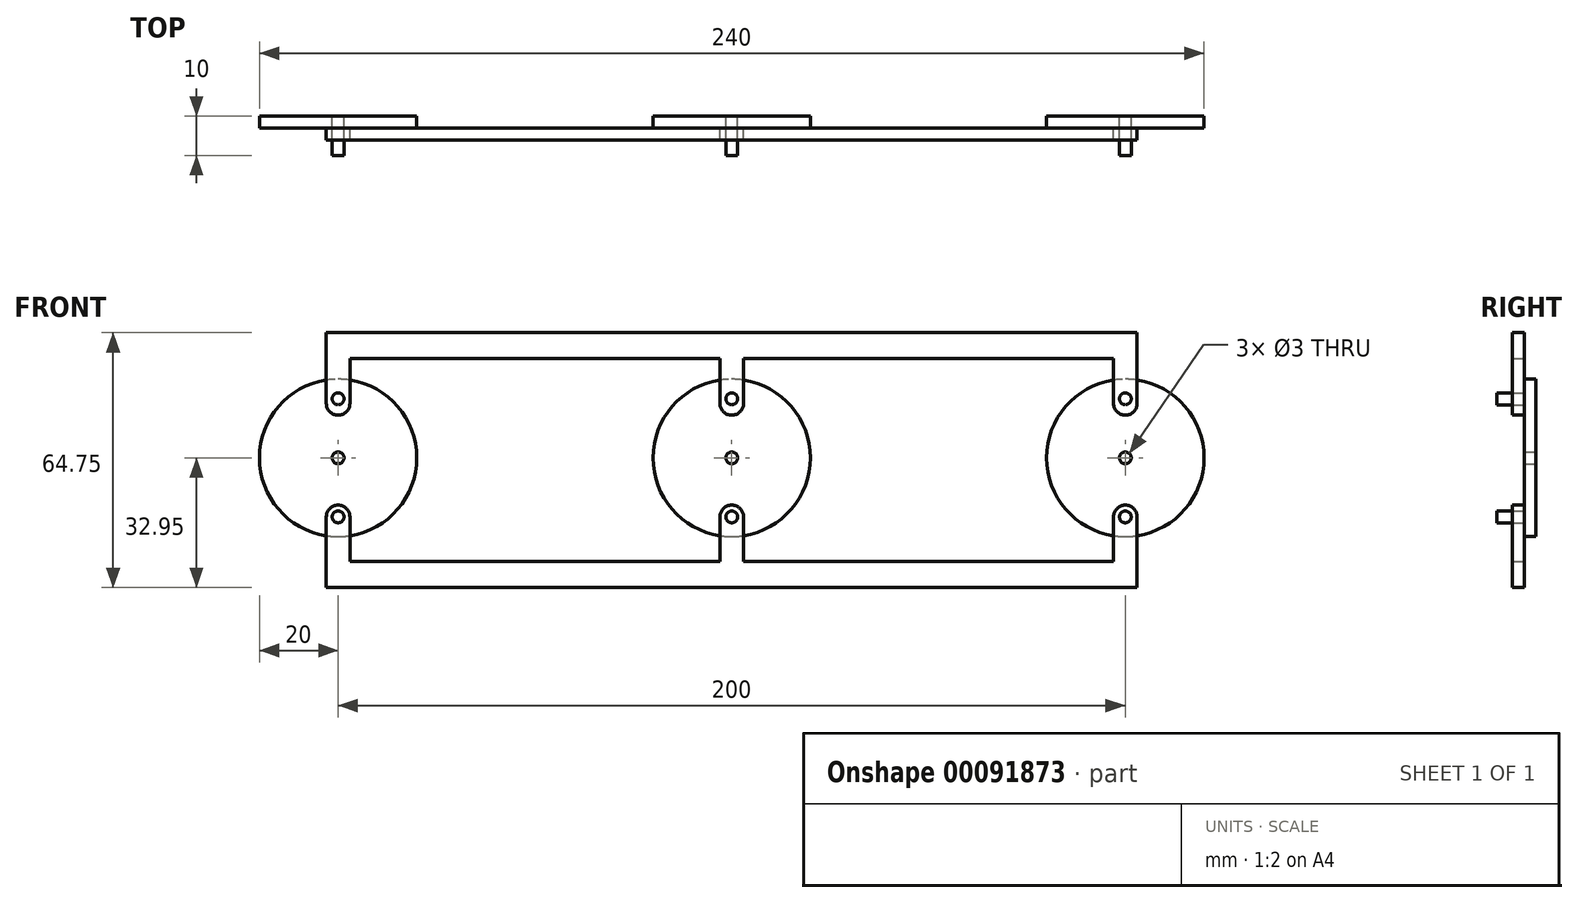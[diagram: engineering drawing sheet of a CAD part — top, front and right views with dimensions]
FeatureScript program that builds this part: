
annotation { "Feature Type Name" : "Feature", "Feature Type Description" : "" }
export const myFeature = defineFeature(function(context is Context, id is Id, definition is map)
    precondition{}
    {
        {
            var Q0;
            Q0=qCreatedBy(makeId("Front.planeOp"),FACE);
            var sketch = newSketch(context, id + "F0", { "sketchPlane" : qUnion([Q0])});
            skLineSegment(sketch, "E0", {"start": v(0, 45.39) * mm, "end": v(-100, 45.39) * mm});
            skCircle(sketch, "E1", {"center": v(-100, 0) * mm, "radius": 20 * mm});
            skCircle(sketch, "E2.1.0.0", {"center": v(0, 0) * mm, "radius": 20 * mm});
            skCircle(sketch, "E2.2.0.0", {"center": v(100, 0) * mm, "radius": 20 * mm});
            skLineSegment(sketch, "E2.direction1", {"start": v(-100, 0) * mm, "end": v(0, 0) * mm, "construction": true});
            skCircle(sketch, "E3", {"center": v(-100, 15) * mm, "radius": 1.5 * mm});
            skCircle(sketch, "E4", {"center": v(-100, -15) * mm, "radius": 1.5 * mm});
            skCircle(sketch, "E5.1.0.0", {"center": v(0, 15) * mm, "radius": 1.5 * mm});
            skCircle(sketch, "E5.1.0.1", {"center": v(0, -15) * mm, "radius": 1.5 * mm});
            skCircle(sketch, "E5.2.0.0", {"center": v(100, 15) * mm, "radius": 1.5 * mm});
            skCircle(sketch, "E5.2.0.1", {"center": v(100, -15) * mm, "radius": 1.5 * mm});
            skLineSegment(sketch, "E5.direction1", {"start": v(-100, 15) * mm, "end": v(0, 15) * mm, "construction": true});
            skCircle(sketch, "E6", {"center": v(-100, 0) * mm, "radius": 1.5 * mm});
            skCircle(sketch, "E7.1.0.0", {"center": v(0, 0) * mm, "radius": 1.5 * mm});
            skCircle(sketch, "E7.2.0.0", {"center": v(100, 0) * mm, "radius": 1.5 * mm});
            skSolve(sketch);
        }
        {
            var Q0;
            Q0 = qSketchRegion(id + "F0", true);
            extrude(context, id + "F1", {"entities" : qUnion([Q0]), "depth" : 3 * mm});
        }
        {
            var Q0;
            Q0=makeQuery(id+"F0.imprint","IMPRINT",FACE,{"disambiguationData":[TD([[makeQuery(id+"F0.imprint","IMPRINT",EDGE,{"derivedFrom":sQuery(id+"F0.wireOp",EDGE,"E3")}),1.0]])]});
            var Q1;
            Q1=makeQuery(id+"F0.imprint","IMPRINT",FACE,{"disambiguationData":[TD([[makeQuery(id+"F0.imprint","IMPRINT",EDGE,{"derivedFrom":sQuery(id+"F0.wireOp",EDGE,"E4")}),1.0]])]});
            var Q2;
            Q2=makeQuery(id+"F0.imprint","IMPRINT",FACE,{"disambiguationData":[TD([[makeQuery(id+"F0.imprint","IMPRINT",EDGE,{"derivedFrom":sQuery(id+"F0.wireOp",EDGE,"E5.2.0.0")}),1.0]])]});
            var Q3;
            Q3=makeQuery(id+"F0.imprint","IMPRINT",FACE,{"disambiguationData":[TD([[makeQuery(id+"F0.imprint","IMPRINT",EDGE,{"derivedFrom":sQuery(id+"F0.wireOp",EDGE,"E5.2.0.1")}),1.0]])]});
            var Q4;
            Q4=makeQuery(id+"F0.imprint","IMPRINT",FACE,{"disambiguationData":[TD([[makeQuery(id+"F0.imprint","IMPRINT",EDGE,{"derivedFrom":sQuery(id+"F0.wireOp",EDGE,"E5.1.0.1")}),1.0]])]});
            var Q5;
            Q5=makeQuery(id+"F0.imprint","IMPRINT",FACE,{"disambiguationData":[TD([[makeQuery(id+"F0.imprint","IMPRINT",EDGE,{"derivedFrom":sQuery(id+"F0.wireOp",EDGE,"E5.1.0.0")}),1.0]])]});
            extrude(context, id + "F2", {"entities" : qUnion([Q0, Q1, Q2, Q3, Q4, Q5]), "operationType" : NewBodyOperationType.ADD, "depth" : 10 * mm});
        }
        {
            var Q0;
            Q0=makeQuery(id+"F1.opExtrude","CAP_FACE",FACE,{"disambiguationData":[OSD([sQuery(id+"F0.wireOp",EDGE,"E1"),sQuery(id+"F0.wireOp",EDGE,"E3"),sQuery(id+"F0.wireOp",EDGE,"E4"),sQuery(id+"F0.wireOp",EDGE,"E6")])],"isStart":false});
            var sketch = newSketch(context, id + "F3", { "sketchPlane" : qUnion([Q0])});
            skLineSegment(sketch, "E8", {"start": v(0, 0) * mm, "end": v(0, -15) * mm});
            skCircle(sketch, "E9", {"center": v(-100, -15) * mm, "radius": 3 * mm});
            skLineSegment(sketch, "E10.bottom", {"start": v(-97, -15) * mm, "end": v(-103, -15) * mm});
            skLineSegment(sketch, "E10.top", {"start": v(-97, -32.95) * mm, "end": v(-103, -32.95) * mm});
            skLineSegment(sketch, "E10.left", {"start": v(-97, -15) * mm, "end": v(-97, -32.95) * mm});
            skLineSegment(sketch, "E10.right", {"start": v(-103, -15) * mm, "end": v(-103, -32.95) * mm});
            skPoint(sketch, "E10.middle", {"position": v(-100, -23.97) * mm});
            skLineSegment(sketch, "E11.1.0.0", {"start": v(3, -15) * mm, "end": v(3, -32.95) * mm});
            skLineSegment(sketch, "E11.1.0.1", {"start": v(3, -32.95) * mm, "end": v(-3, -32.95) * mm});
            skLineSegment(sketch, "E11.1.0.2", {"start": v(-3, -15) * mm, "end": v(-3, -32.95) * mm});
            skCircle(sketch, "E11.1.0.3", {"center": v(0, -15) * mm, "radius": 3 * mm});
            skLineSegment(sketch, "E11.2.0.0", {"start": v(103, -15) * mm, "end": v(103, -32.95) * mm});
            skLineSegment(sketch, "E11.2.0.1", {"start": v(103, -32.95) * mm, "end": v(97, -32.95) * mm});
            skLineSegment(sketch, "E11.2.0.2", {"start": v(97, -15) * mm, "end": v(97, -32.95) * mm});
            skCircle(sketch, "E11.2.0.3", {"center": v(100, -15) * mm, "radius": 3 * mm});
            skLineSegment(sketch, "E11.direction1", {"start": v(-97, -32.95) * mm, "end": v(3, -32.95) * mm, "construction": true});
            skLineSegment(sketch, "E12.bottom", {"start": v(-103, -32.95) * mm, "end": v(103, -32.95) * mm});
            skLineSegment(sketch, "E12.top", {"start": v(-103, -26.36) * mm, "end": v(103, -26.36) * mm});
            skLineSegment(sketch, "E12.left", {"start": v(-103, -32.95) * mm, "end": v(-103, -26.36) * mm});
            skLineSegment(sketch, "E12.right", {"start": v(103, -32.95) * mm, "end": v(103, -26.36) * mm});
            skSolve(sketch);
        }
        {
            var Q0;
            Q0 = qSketchRegion(id + "F3", true);
            extrude(context, id + "F4", {"entities" : qUnion([Q0]), "depth" : 3 * mm});
        }
        {
            var Q0;
            Q0=makeQuery(id+"F4.opExtrude","SWEPT_BODY",BODY,{"disambiguationData":[OSD([sQuery(id+"F3.wireOp",EDGE,"E9"),sQuery(id+"F3.wireOp",EDGE,"E10.left"),sQuery(id+"F3.wireOp",EDGE,"E10.right"),sQuery(id+"F3.wireOp",EDGE,"E11.1.0.0"),sQuery(id+"F3.wireOp",EDGE,"E11.1.0.2"),sQuery(id+"F3.wireOp",EDGE,"E11.1.0.3"),sQuery(id+"F3.wireOp",EDGE,"E11.2.0.0"),sQuery(id+"F3.wireOp",EDGE,"E11.2.0.2"),sQuery(id+"F3.wireOp",EDGE,"E11.2.0.3"),sQuery(id+"F3.wireOp",EDGE,"E12.bottom"),sQuery(id+"F3.wireOp",EDGE,"E12.top"),sQuery(id+"F3.wireOp",EDGE,"E12.left"),sQuery(id+"F3.wireOp",EDGE,"E12.right")])]});
            var Q1;
            {var subQ0=sQuery(id+"F3.wireOp",EDGE,"E12.top");Q1=makeQuery(id+"F4.opExtrude","SWEPT_FACE",FACE,{"disambiguationData":[OSD([subQ0]),TDD([makeQuery(id+"F3.imprint","IMPRINT",EDGE,{"disambiguationData":[TD([[makeQuery(id+"F3.imprint","INTERSECT",VERTEX,{"derivedFrom":[sQuery(id+"F3.wireOp",EDGE,"E10.left"),subQ0]}),-1.0]])],"derivedFrom":subQ0})])]});}
            mirror(context, id + "F5", {"entities" : qUnion([Q0]), "mirrorPlane" : qUnion([Q1])});
        }
        {
            var Q0;
            Q0=makeQuery(id+"F5.opPattern","COPY",BODY,{"derivedFrom":makeQuery(id+"F4.opExtrude","SWEPT_BODY",BODY,{"disambiguationData":[OSD([sQuery(id+"F3.wireOp",EDGE,"E9"),sQuery(id+"F3.wireOp",EDGE,"E10.left"),sQuery(id+"F3.wireOp",EDGE,"E10.right"),sQuery(id+"F3.wireOp",EDGE,"E11.1.0.0"),sQuery(id+"F3.wireOp",EDGE,"E11.1.0.2"),sQuery(id+"F3.wireOp",EDGE,"E11.1.0.3"),sQuery(id+"F3.wireOp",EDGE,"E11.2.0.0"),sQuery(id+"F3.wireOp",EDGE,"E11.2.0.2"),sQuery(id+"F3.wireOp",EDGE,"E11.2.0.3"),sQuery(id+"F3.wireOp",EDGE,"E12.bottom"),sQuery(id+"F3.wireOp",EDGE,"E12.top"),sQuery(id+"F3.wireOp",EDGE,"E12.left"),sQuery(id+"F3.wireOp",EDGE,"E12.right")])]}),"instanceName":"1"});
            transform(context, id + "F6", {"entities" : qUnion([Q0]), "transformType" : TransformType.TRANSLATION_3D, "dx" : 0 * mm, "dy" : 0 * mm, "dz" : 51.58 * mm, "makeCopy" : false});
        }
    });
